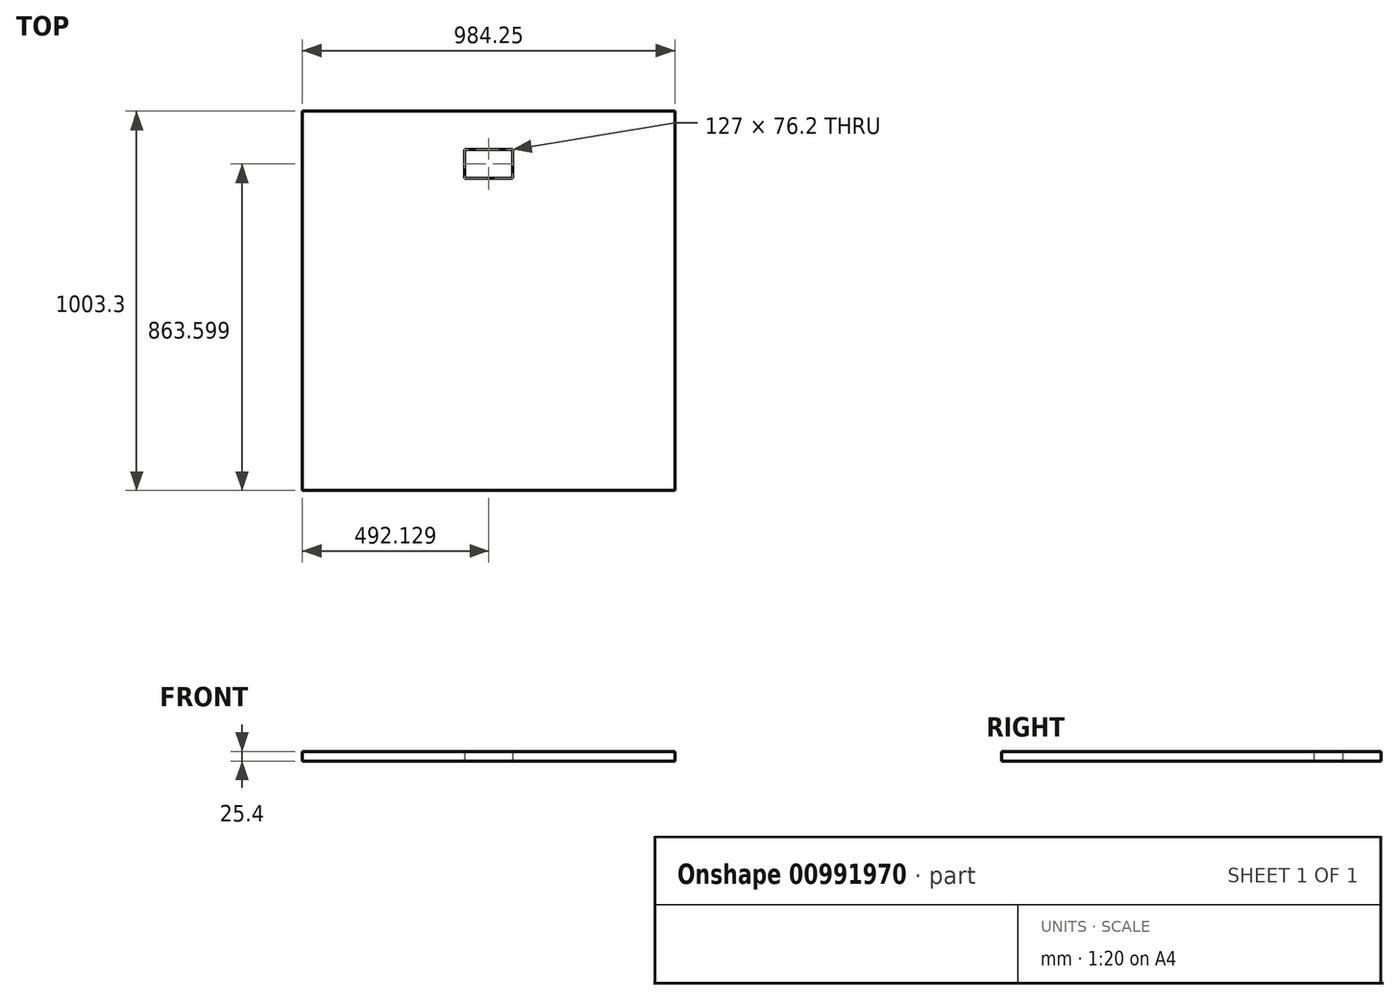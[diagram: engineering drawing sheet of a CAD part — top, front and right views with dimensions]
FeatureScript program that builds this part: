
annotation { "Feature Type Name" : "Feature", "Feature Type Description" : "" }
export const myFeature = defineFeature(function(context is Context, id is Id, definition is map)
    precondition{}
    {
        {
            var Q0;
            Q0=qCreatedBy(makeId("Top.planeOp"),FACE);
            var sketch = newSketch(context, id + "F0", { "sketchPlane" : qUnion([Q0])});
            skLineSegment(sketch, "E0", {"start": v(-76.29, 515.4) * mm, "end": v(-76.29, -487.9) * mm});
            skLineSegment(sketch, "E1", {"start": v(-76.29, -487.9) * mm, "end": v(907.96, -487.9) * mm});
            skLineSegment(sketch, "E2", {"start": v(-76.29, 515.4) * mm, "end": v(907.96, 515.4) * mm});
            skLineSegment(sketch, "E3", {"start": v(907.96, 515.4) * mm, "end": v(907.96, -487.9) * mm});
            skLineSegment(sketch, "E4", {"start": v(352.34, 413.8) * mm, "end": v(352.34, 337.6) * mm});
            skLineSegment(sketch, "E5", {"start": v(352.34, 337.6) * mm, "end": v(479.34, 337.6) * mm});
            skLineSegment(sketch, "E6", {"start": v(479.34, 337.6) * mm, "end": v(479.34, 413.8) * mm});
            skLineSegment(sketch, "E7", {"start": v(352.34, 413.8) * mm, "end": v(479.34, 413.8) * mm});
            skSolve(sketch);
        }
        {
            var Q0;
            Q0 = qSketchRegion(id + "F0", true);
            extrude(context, id + "F1", {"entities" : qUnion([Q0]), "depth" : 6.35 * mm, "offsetDistance" : 25.4 * mm});
        }
        {
            var Q0;
            Q0 = qSketchRegion(id + "F0", true);
            extrude(context, id + "F2", {"entities" : qUnion([Q0]), "operationType" : NewBodyOperationType.ADD, "depth" : 25.4 * mm, "offsetDistance" : 25.4 * mm});
        }
        {
            var Q0;
            Q0 = qSketchRegion(id + "F0", true);
            extrude(context, id + "F3", {"entities" : qUnion([Q0]), "operationType" : NewBodyOperationType.ADD, "depth" : 25.4 * mm, "offsetDistance" : 25.4 * mm});
        }
    });
